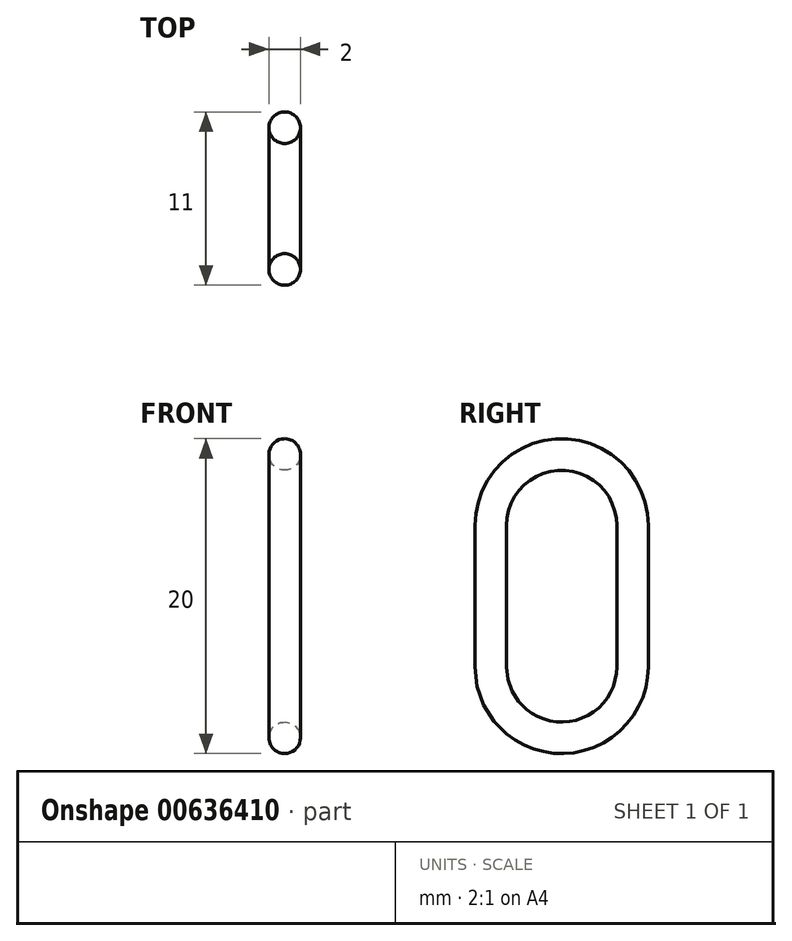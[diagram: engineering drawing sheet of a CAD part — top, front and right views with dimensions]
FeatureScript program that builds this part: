
annotation { "Feature Type Name" : "Feature", "Feature Type Description" : "" }
export const myFeature = defineFeature(function(context is Context, id is Id, definition is map)
    precondition{}
    {
        {
            var Q0;
            Q0=qCreatedBy(makeId("Right.planeOp"),FACE);
            var sketch = newSketch(context, id + "F0", { "sketchPlane" : qUnion([Q0])});
            skArc(sketch, "E0", {"start": v(4.5, 9) * mm, "mid": v(0, 13.5) * mm, "end": v(-4.5, 9) * mm});
            skArc(sketch, "E1", {"start": v(-4.5, 0) * mm, "mid": v(0, -4.5) * mm, "end": v(4.5, 0) * mm});
            skLineSegment(sketch, "E2", {"start": v(-4.5, 0) * mm, "end": v(-4.5, 9) * mm});
            skLineSegment(sketch, "E3", {"start": v(4.5, 9) * mm, "end": v(4.5, 0) * mm});
            skLineSegment(sketch, "E4", {"start": v(0, -4.5) * mm, "end": v(0, 13.5) * mm, "construction": true});
            skSolve(sketch);
        }
        {
            var Q0;
            Q0=qCreatedBy(makeId("Top.planeOp"),FACE);
            var sketch = newSketch(context, id + "F1", { "sketchPlane" : qUnion([Q0])});
            skPoint(sketch, "E5.0", {"position": v(0, 4.5) * mm});
            skCircle(sketch, "E6", {"center": v(0, 4.5) * mm, "radius": 1 * mm});
            skSolve(sketch);
        }
        {
            var Q0;
            Q0=makeQuery(id+"F1.imprint","IMPRINT",FACE,{"disambiguationData":[TD([[makeQuery(id+"F1.imprint","IMPRINT",EDGE,{"derivedFrom":sQuery(id+"F1.wireOp",EDGE,"E6")}),1.0]])]});
            var Q1;
            Q1=sQuery(id+"F0.wireOp",EDGE,"E1");
            var Q2;
            Q2=sQuery(id+"F0.wireOp",EDGE,"E2");
            var Q3;
            Q3=sQuery(id+"F0.wireOp",EDGE,"E0");
            var Q4;
            Q4=sQuery(id+"F0.wireOp",EDGE,"E3");
            sweep(context, id + "F2", {"profiles" : qUnion([Q0]), "path" : qUnion([Q1, Q2, Q3, Q4])});
        }
    });
